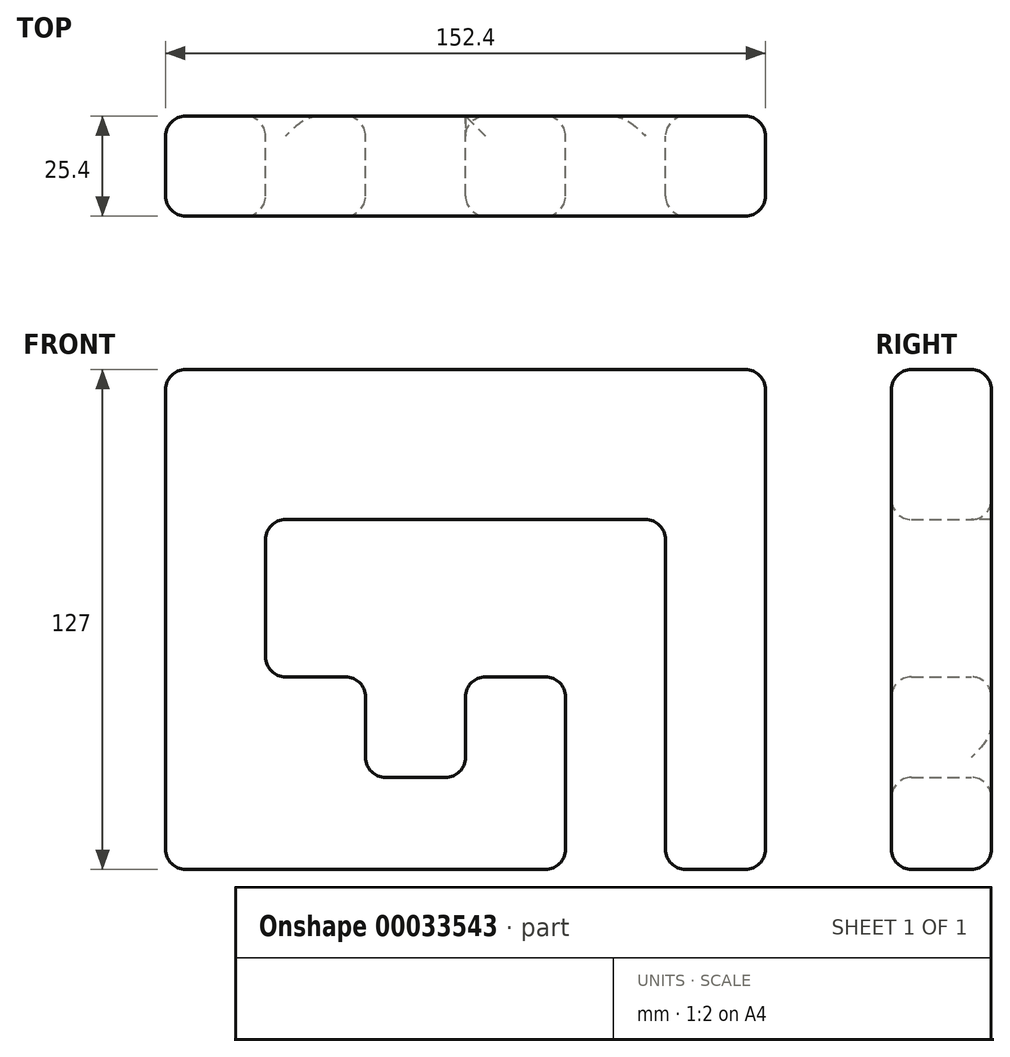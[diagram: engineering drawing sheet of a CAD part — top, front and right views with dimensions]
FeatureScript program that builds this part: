
annotation { "Feature Type Name" : "Feature", "Feature Type Description" : "" }
export const myFeature = defineFeature(function(context is Context, id is Id, definition is map)
    precondition{}
    {
        {
            var Q0;
            Q0=qCreatedBy(makeId("Front.planeOp"),FACE);
            var sketch = newSketch(context, id + "F0", { "sketchPlane" : qUnion([Q0])});
            skLineSegment(sketch, "E0", {"start": v(0, 0) * mm, "end": v(0, -127) * mm});
            skLineSegment(sketch, "E1", {"start": v(0, -127) * mm, "end": v(101.6, -127) * mm});
            skLineSegment(sketch, "E2", {"start": v(101.6, -127) * mm, "end": v(101.6, -78.06) * mm});
            skLineSegment(sketch, "E3", {"start": v(101.6, -78.06) * mm, "end": v(76.2, -78.06) * mm});
            skLineSegment(sketch, "E4", {"start": v(76.2, -78.06) * mm, "end": v(76.2, -103.64) * mm});
            skLineSegment(sketch, "E5", {"start": v(76.2, -103.64) * mm, "end": v(50.8, -103.64) * mm});
            skLineSegment(sketch, "E6", {"start": v(50.8, -103.64) * mm, "end": v(50.8, -78.06) * mm});
            skLineSegment(sketch, "E7", {"start": v(50.8, -78.06) * mm, "end": v(25.4, -78.06) * mm});
            skLineSegment(sketch, "E8", {"start": v(25.4, -78.06) * mm, "end": v(25.4, -38.1) * mm});
            skLineSegment(sketch, "E9", {"start": v(25.4, -38.1) * mm, "end": v(127, -38.1) * mm});
            skLineSegment(sketch, "E10", {"start": v(127, -38.1) * mm, "end": v(127, -127) * mm});
            skLineSegment(sketch, "E11", {"start": v(127, -127) * mm, "end": v(152.4, -127) * mm});
            skLineSegment(sketch, "E12", {"start": v(152.4, -127) * mm, "end": v(152.4, 0) * mm});
            skLineSegment(sketch, "E13", {"start": v(152.4, 0) * mm, "end": v(0, 0) * mm});
            skSolve(sketch);
        }
        {
            var Q0;
            Q0=makeQuery(id+"F0.imprint","IMPRINT",FACE,{"disambiguationData":[TD([[makeQuery(id+"F0.imprint","IMPRINT",EDGE,{"derivedFrom":sQuery(id+"F0.wireOp",EDGE,"E0")}),1.0]])]});
            extrude(context, id + "F1", {"entities" : qUnion([Q0]), "endBound" : BoundingType.SYMMETRIC, "depth" : 25.4 * mm});
        }
        {
            var Q0;
            Q0=makeQuery(id+"F1.opExtrude","CAP_EDGE",EDGE,{"disambiguationData":[OSD([sQuery(id+"F0.wireOp",EDGE,"E13")])],"isStart":false});
            var Q1;
            Q1=makeQuery(id+"F1.opExtrude","CAP_EDGE",EDGE,{"disambiguationData":[OSD([sQuery(id+"F0.wireOp",EDGE,"E13")])],"isStart":true});
            var Q2;
            Q2=makeQuery(id+"F1.opExtrude","SWEPT_EDGE",EDGE,{"disambiguationData":[OSD([sQuery(id+"F0.wireOp",EDGE,"E12"),sQuery(id+"F0.wireOp",EDGE,"E13")])]});
            var Q3;
            Q3=makeQuery(id+"F1.opExtrude","SWEPT_EDGE",EDGE,{"disambiguationData":[OSD([sQuery(id+"F0.wireOp",EDGE,"E0"),sQuery(id+"F0.wireOp",EDGE,"E13")])]});
            var Q4;
            Q4=makeQuery(id+"F1.opExtrude","CAP_EDGE",EDGE,{"disambiguationData":[OSD([sQuery(id+"F0.wireOp",EDGE,"E11")])],"isStart":false});
            var Q5;
            Q5=makeQuery(id+"F1.opExtrude","SWEPT_EDGE",EDGE,{"disambiguationData":[OSD([sQuery(id+"F0.wireOp",EDGE,"E11"),sQuery(id+"F0.wireOp",EDGE,"E12")])]});
            var Q6;
            Q6=makeQuery(id+"F1.opExtrude","SWEPT_EDGE",EDGE,{"disambiguationData":[OSD([sQuery(id+"F0.wireOp",EDGE,"E10"),sQuery(id+"F0.wireOp",EDGE,"E11")])]});
            var Q7;
            Q7=makeQuery(id+"F1.opExtrude","CAP_EDGE",EDGE,{"disambiguationData":[OSD([sQuery(id+"F0.wireOp",EDGE,"E11")])],"isStart":true});
            var Q8;
            Q8=makeQuery(id+"F1.opExtrude","SWEPT_EDGE",EDGE,{"disambiguationData":[OSD([sQuery(id+"F0.wireOp",EDGE,"E1"),sQuery(id+"F0.wireOp",EDGE,"E2")])]});
            var Q9;
            Q9=makeQuery(id+"F1.opExtrude","CAP_EDGE",EDGE,{"disambiguationData":[OSD([sQuery(id+"F0.wireOp",EDGE,"E1")])],"isStart":false});
            var Q10;
            Q10=makeQuery(id+"F1.opExtrude","CAP_EDGE",EDGE,{"disambiguationData":[OSD([sQuery(id+"F0.wireOp",EDGE,"E2")])],"isStart":false});
            var Q11;
            Q11=makeQuery(id+"F1.opExtrude","CAP_EDGE",EDGE,{"disambiguationData":[OSD([sQuery(id+"F0.wireOp",EDGE,"E2")])],"isStart":true});
            var Q12;
            Q12=makeQuery(id+"F1.opExtrude","SWEPT_EDGE",EDGE,{"disambiguationData":[OSD([sQuery(id+"F0.wireOp",EDGE,"E2"),sQuery(id+"F0.wireOp",EDGE,"E3")])]});
            var Q13;
            Q13=makeQuery(id+"F1.opExtrude","CAP_EDGE",EDGE,{"disambiguationData":[OSD([sQuery(id+"F0.wireOp",EDGE,"E1")])],"isStart":true});
            var Q14;
            Q14=makeQuery(id+"F1.opExtrude","SWEPT_EDGE",EDGE,{"disambiguationData":[OSD([sQuery(id+"F0.wireOp",EDGE,"E0"),sQuery(id+"F0.wireOp",EDGE,"E1")])]});
            var Q15;
            Q15=makeQuery(id+"F1.opExtrude","CAP_EDGE",EDGE,{"disambiguationData":[OSD([sQuery(id+"F0.wireOp",EDGE,"E5")])],"isStart":false});
            var Q16;
            Q16=makeQuery(id+"F1.opExtrude","CAP_EDGE",EDGE,{"disambiguationData":[OSD([sQuery(id+"F0.wireOp",EDGE,"E4")])],"isStart":false});
            var Q17;
            Q17=makeQuery(id+"F1.opExtrude","CAP_EDGE",EDGE,{"disambiguationData":[OSD([sQuery(id+"F0.wireOp",EDGE,"E6")])],"isStart":false});
            var Q18;
            Q18=makeQuery(id+"F1.opExtrude","SWEPT_EDGE",EDGE,{"disambiguationData":[OSD([sQuery(id+"F0.wireOp",EDGE,"E6"),sQuery(id+"F0.wireOp",EDGE,"E7")])]});
            var Q19;
            Q19=makeQuery(id+"F1.opExtrude","CAP_EDGE",EDGE,{"disambiguationData":[OSD([sQuery(id+"F0.wireOp",EDGE,"E6")])],"isStart":true});
            var Q20;
            Q20=makeQuery(id+"F1.opExtrude","CAP_EDGE",EDGE,{"disambiguationData":[OSD([sQuery(id+"F0.wireOp",EDGE,"E5")])],"isStart":true});
            var Q21;
            Q21=makeQuery(id+"F1.opExtrude","SWEPT_EDGE",EDGE,{"disambiguationData":[OSD([sQuery(id+"F0.wireOp",EDGE,"E3"),sQuery(id+"F0.wireOp",EDGE,"E4")])]});
            var Q22;
            Q22=makeQuery(id+"F1.opExtrude","CAP_EDGE",EDGE,{"disambiguationData":[OSD([sQuery(id+"F0.wireOp",EDGE,"E3")])],"isStart":true});
            var Q23;
            Q23=makeQuery(id+"F1.opExtrude","CAP_EDGE",EDGE,{"disambiguationData":[OSD([sQuery(id+"F0.wireOp",EDGE,"E10")])],"isStart":false});
            var Q24;
            Q24=makeQuery(id+"F1.opExtrude","CAP_EDGE",EDGE,{"disambiguationData":[OSD([sQuery(id+"F0.wireOp",EDGE,"E10")])],"isStart":true});
            var Q25;
            Q25=makeQuery(id+"F1.opExtrude","CAP_EDGE",EDGE,{"disambiguationData":[OSD([sQuery(id+"F0.wireOp",EDGE,"E9")])],"isStart":false});
            var Q26;
            Q26=makeQuery(id+"F1.opExtrude","CAP_EDGE",EDGE,{"disambiguationData":[OSD([sQuery(id+"F0.wireOp",EDGE,"E8")])],"isStart":false});
            var Q27;
            Q27=makeQuery(id+"F1.opExtrude","CAP_EDGE",EDGE,{"disambiguationData":[OSD([sQuery(id+"F0.wireOp",EDGE,"E7")])],"isStart":false});
            var Q28;
            Q28=makeQuery(id+"F1.opExtrude","CAP_EDGE",EDGE,{"disambiguationData":[OSD([sQuery(id+"F0.wireOp",EDGE,"E0")])],"isStart":false});
            var Q29;
            Q29=makeQuery(id+"F1.opExtrude","CAP_EDGE",EDGE,{"disambiguationData":[OSD([sQuery(id+"F0.wireOp",EDGE,"E3")])],"isStart":false});
            var Q30;
            Q30=makeQuery(id+"F1.opExtrude","CAP_EDGE",EDGE,{"disambiguationData":[OSD([sQuery(id+"F0.wireOp",EDGE,"E7")])],"isStart":true});
            var Q31;
            Q31=makeQuery(id+"F1.opExtrude","SWEPT_EDGE",EDGE,{"disambiguationData":[OSD([sQuery(id+"F0.wireOp",EDGE,"E7"),sQuery(id+"F0.wireOp",EDGE,"E8")])]});
            var Q32;
            Q32=makeQuery(id+"F1.opExtrude","CAP_EDGE",EDGE,{"disambiguationData":[OSD([sQuery(id+"F0.wireOp",EDGE,"E0")])],"isStart":true});
            var Q33;
            Q33=makeQuery(id+"F1.opExtrude","SWEPT_FACE",FACE,{"disambiguationData":[OSD([sQuery(id+"F0.wireOp",EDGE,"E8")])]});
            var Q34;
            Q34=makeQuery(id+"F1.opExtrude","SWEPT_FACE",FACE,{"disambiguationData":[OSD([sQuery(id+"F0.wireOp",EDGE,"E10")])]});
            var Q35;
            Q35=makeQuery(id+"F1.opExtrude","CAP_EDGE",EDGE,{"disambiguationData":[OSD([sQuery(id+"F0.wireOp",EDGE,"E12")])],"isStart":false});
            var Q36;
            Q36=makeQuery(id+"F1.opExtrude","CAP_EDGE",EDGE,{"disambiguationData":[OSD([sQuery(id+"F0.wireOp",EDGE,"E12")])],"isStart":true});
            var Q37;
            Q37=makeQuery(id+"F1.opExtrude","SWEPT_EDGE",EDGE,{"disambiguationData":[OSD([sQuery(id+"F0.wireOp",EDGE,"E4"),sQuery(id+"F0.wireOp",EDGE,"E5")])]});
            var Q38;
            Q38=makeQuery(id+"F1.opExtrude","SWEPT_EDGE",EDGE,{"disambiguationData":[OSD([sQuery(id+"F0.wireOp",EDGE,"E5"),sQuery(id+"F0.wireOp",EDGE,"E6")])]});
            fillet(context, id + "F2", {"entities" : qUnion([Q0, Q1, Q2, Q3, Q4, Q5, Q6, Q7, Q8, Q9, Q10, Q11, Q12, Q13, Q14, Q15, Q16, Q17, Q18, Q19, Q20, Q21, Q22, Q23, Q24, Q25, Q26, Q27, Q28, Q29, Q30, Q31, Q32, Q33, Q34, Q35, Q36, Q37, Q38]), "radius" : 5.08 * mm, "tangentPropagation" : true, "allowEdgeOverflow" : false});
        }
    });
